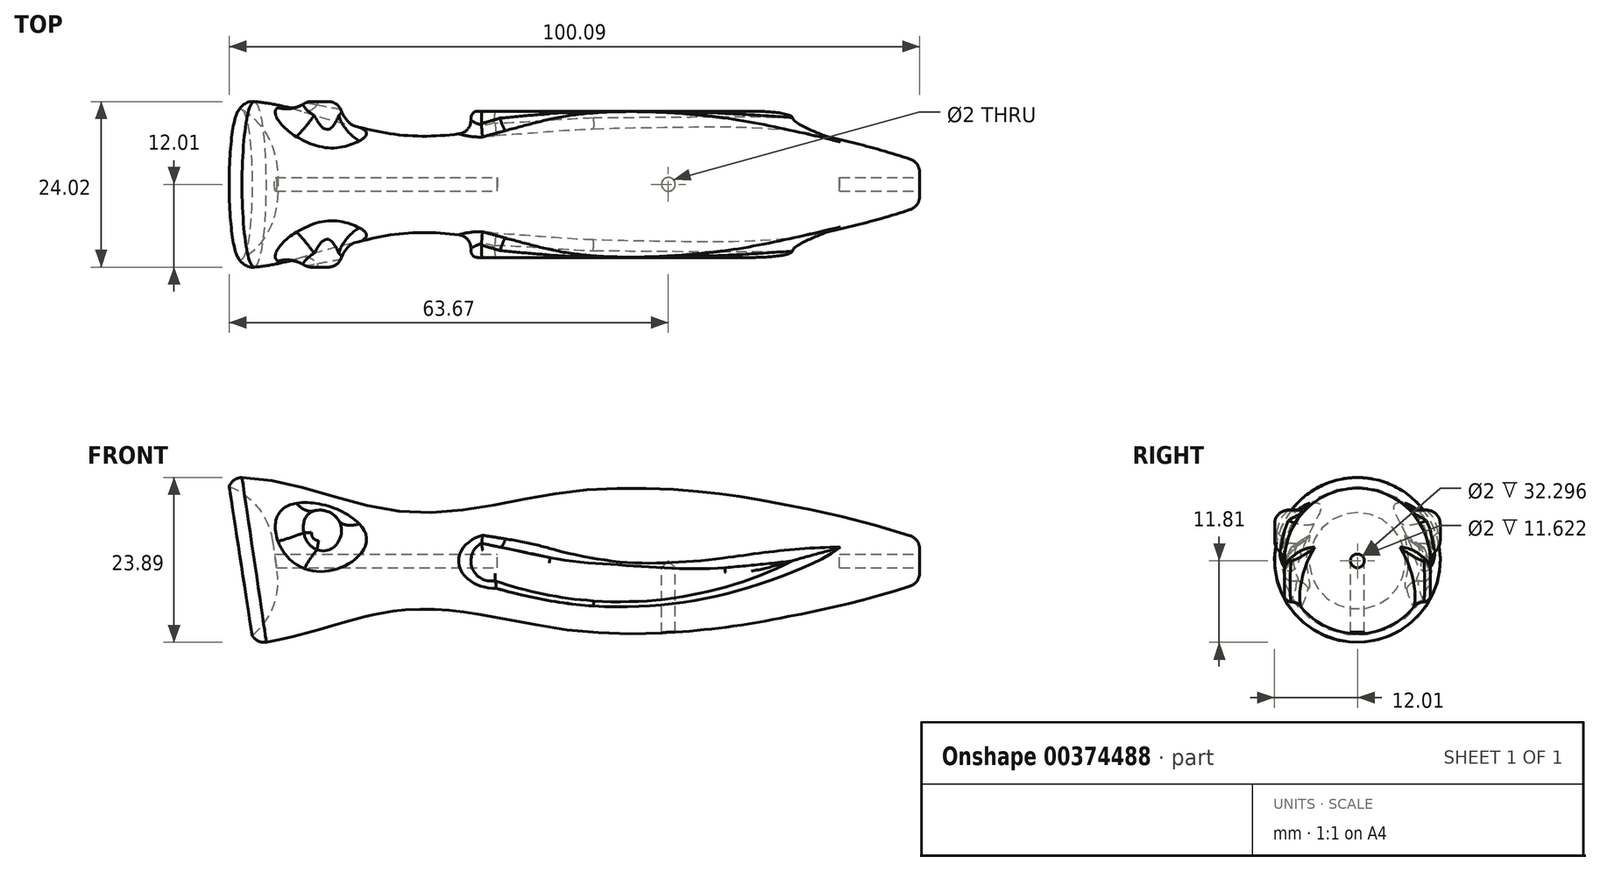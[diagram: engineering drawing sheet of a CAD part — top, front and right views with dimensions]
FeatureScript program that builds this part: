
annotation { "Feature Type Name" : "Feature", "Feature Type Description" : "" }
export const myFeature = defineFeature(function(context is Context, id is Id, definition is map)
    precondition{}
    {
        {
            var Q0;
            Q0=qCreatedBy(makeId("Front.planeOp"),FACE);
            var sketch = newSketch(context, id + "F0", { "sketchPlane" : qUnion([Q0])});
            skLineSegment(sketch, "E0", {"start": v(-64.17, 0) * mm, "end": v(44.05, 0) * mm});
            skFitSpline(sketch, "E1", {"points": [v(-64.13, 11.91) * mm, v(-39.28, 7.2) * mm, v(-14.5, 10.01) * mm, v(5.16, 9.98) * mm, v(16.36, 8.27) * mm, v(44.05, 0) * mm], "startDerivative": vector(102.28, 15.68) * mm, "endDerivative": vector(118.61, -59.18) * mm});
            skLineSegment(sketch, "E2.bottom", {"start": v(36.42, 9.8) * mm, "end": v(56.27, 9.8) * mm});
            skLineSegment(sketch, "E2.top", {"start": v(36.42, -4.91) * mm, "end": v(56.27, -4.91) * mm});
            skLineSegment(sketch, "E2.left", {"start": v(36.42, 9.8) * mm, "end": v(36.42, -4.91) * mm});
            skLineSegment(sketch, "E2.right", {"start": v(56.27, 9.8) * mm, "end": v(56.27, -4.91) * mm});
            skLineSegment(sketch, "E3", {"start": v(-64.13, 11.91) * mm, "end": v(-64.17, 0) * mm});
            skSolve(sketch);
        }
        {
            var Q0;
            {var subQ0=sQuery(id+"F0.wireOp",EDGE,"E3");Q0=makeQuery(id+"F0.imprint","IMPRINT",FACE,{"disambiguationData":[TD([[makeQuery(id+"F0.imprint","IMPRINT",EDGE,{"derivedFrom":subQ0}),1.0]])]});}
            var Q1;
            Q1 = qSketchRegion(id + "F2", true);
            var Q2;
            Q2=sQuery(id+"F0.wireOp",EDGE,"E0");
            revolve(context, id + "F1", {"surfaceOperationType" : NewSurfaceOperationType.NEW, "entities" : qUnion([Q0, Q1]), "axis" : qUnion([Q2]), "revolveType" : RevolveType.FULL});
        }
        {
            var Q0;
            Q0=qCreatedBy(makeId("Front.planeOp"),FACE);
            var sketch = newSketch(context, id + "F2", { "sketchPlane" : qUnion([Q0])});
            skLineSegment(sketch, "E4", {"start": v(-65.45, 22.3) * mm, "end": v(-56.64, -34.7) * mm});
            skLineSegment(sketch, "E5", {"start": v(-56.64, -34.7) * mm, "end": v(-81.8, -34.7) * mm});
            skLineSegment(sketch, "E6", {"start": v(-81.8, -34.7) * mm, "end": v(-65.45, 22.3) * mm});
            skSolve(sketch);
        }
        {
            var Q0;
            Q0=makeQuery(id+"F2.imprint","IMPRINT",FACE,{"disambiguationData":[TD([[makeQuery(id+"F2.imprint","IMPRINT",EDGE,{"derivedFrom":sQuery(id+"F2.wireOp",EDGE,"E4")}),-1.0]])]});
            extrude(context, id + "F3", {"entities" : qUnion([Q0]), "operationType" : NewBodyOperationType.REMOVE, "endBound" : BoundingType.SYMMETRIC, "oppositeDirection" : true, "offsetDistance" : 25 * mm, "depth" : 32.6 * mm});
        }
        {
            var Q0;
            Q0=makeQuery(id+"F3.boolean.opBoolean","COPY",FACE,{"derivedFrom":makeQuery(id+"F3.opExtrude","SWEPT_FACE",FACE,{"disambiguationData":[OSD([sQuery(id+"F2.wireOp",EDGE,"E4")])]})});
            var sketch = newSketch(context, id + "F4", { "sketchPlane" : qUnion([Q0])});
            skCircle(sketch, "E7", {"center": v(0, 9.47) * mm, "radius": 10.92 * mm});
            skSolve(sketch);
        }
        {
            var Q0;
            Q0=qSketchRegion(id+"F4",true);
            extrude(context, id + "F5", {"entities" : qUnion([Q0]), "operationType" : NewBodyOperationType.REMOVE, "oppositeDirection" : true, "offsetDistance" : 25 * mm, "depth" : 5 * mm});
        }
        {
            var Q0;
            Q0=makeQuery(id+"F5.boolean.opBoolean","COPY",EDGE,{"derivedFrom":makeQuery(id+"F5.opExtrude","CAP_EDGE",EDGE,{"disambiguationData":[OSD([sQuery(id+"F4.wireOp",EDGE,"E7")])],"isStart":false})});
            fillet(context, id + "F6", {"entities" : qUnion([Q0]), "radius" : 10 * mm, "tangentPropagation" : true, "defaultsChanged" : false, "vertexSettings" : [], "allowEdgeOverflow" : false});
        }
        {
            var Q0;
            Q0=qCreatedBy(makeId("Front.planeOp"),FACE);
            var sketch = newSketch(context, id + "F7", { "sketchPlane" : qUnion([Q0])});
            skCircle(sketch, "E8", {"center": v(-50.52, 4.14) * mm, "radius": 3.23 * mm});
            skSolve(sketch);
        }
        {
            var Q0;
            Q0=qSketchRegion(id+"F7",true);
            extrude(context, id + "F8", {"entities" : qUnion([Q0]), "operationType" : NewBodyOperationType.ADD, "endBound" : BoundingType.SYMMETRIC, "oppositeDirection" : true, "offsetDistance" : 25 * mm, "depth" : 24 * mm});
        }
        {
            var Q0;
            Q0=makeQuery(id+"F8.opExtrude","CAP_EDGE",EDGE,{"disambiguationData":[OSD([sQuery(id+"F7.wireOp",EDGE,"E8")])],"isStart":true});
            var Q1;
            Q1=makeQuery(id+"F8.opExtrude","CAP_EDGE",EDGE,{"disambiguationData":[OSD([sQuery(id+"F7.wireOp",EDGE,"E8")])],"isStart":false});
            fillet(context, id + "F9", {"entities" : qUnion([Q0, Q1]), "radius" : 2 * mm, "tangentPropagation" : true, "defaultsChanged" : false, "vertexSettings" : [], "allowEdgeOverflow" : false});
        }
        {
            var Q0;
            Q0=makeQuery(id+"F8.boolean.opBoolean","INTERSECT",EDGE,{"disambiguationData":[OD(0.0)],"derivedFrom":[makeQuery(id+"F1.opRevolve","SWEPT_FACE",FACE,{"disambiguationData":[OSD([sQuery(id+"F0.wireOp",EDGE,"E1")])]}),makeQuery(id+"F8.opExtrude","SWEPT_FACE",FACE,{"disambiguationData":[OSD([sQuery(id+"F7.wireOp",EDGE,"E8")])]})]});
            var Q1;
            Q1=makeQuery(id+"F8.boolean.opBoolean","INTERSECT",EDGE,{"disambiguationData":[OD(1.0)],"derivedFrom":[makeQuery(id+"F1.opRevolve","SWEPT_FACE",FACE,{"disambiguationData":[OSD([sQuery(id+"F0.wireOp",EDGE,"E1")])]}),makeQuery(id+"F8.opExtrude","SWEPT_FACE",FACE,{"disambiguationData":[OSD([sQuery(id+"F7.wireOp",EDGE,"E8")])]})]});
            fillet(context, id + "F10", {"entities" : qUnion([Q0, Q1]), "radius" : 5 * mm, "tangentPropagation" : true, "defaultsChanged" : false, "vertexSettings" : [], "allowEdgeOverflow" : false});
        }
        {
            var Q0;
            Q0=qCreatedBy(makeId("Front.planeOp"),FACE);
            var sketch = newSketch(context, id + "F11", { "sketchPlane" : qUnion([Q0])});
            skArc(sketch, "E9", {"start": v(-27.1, 2.57) * mm, "mid": v(-28.45, -0.99) * mm, "end": v(-25.16, -2.88) * mm});
            skArc(sketch, "E10", {"start": v(-25.16, -2.88) * mm, "mid": v(-3.29, -5.8) * mm, "end": v(18, 0) * mm});
            skArc(sketch, "E11", {"start": v(-27.1, 2.57) * mm, "mid": v(-4.66, -0.58) * mm, "end": v(18, 0) * mm});
            skSolve(sketch);
        }
        {
            var Q0;
            Q0=qSketchRegion(id+"F11",true);
            extrude(context, id + "F12", {"entities" : qUnion([Q0]), "operationType" : NewBodyOperationType.ADD, "endBound" : BoundingType.SYMMETRIC, "depth" : 21.2 * mm});
        }
        {
            var Q0;
            Q0=makeQuery(id+"F12.opExtrude","CAP_EDGE",EDGE,{"disambiguationData":[OSD([sQuery(id+"F11.wireOp",EDGE,"a57460a2-1e1d-4164-8bf6-132b992fdc75")])],"isStart":false});
            var Q1;
            Q1=makeQuery(id+"F12.opExtrude","CAP_EDGE",EDGE,{"disambiguationData":[OSD([sQuery(id+"F11.wireOp",EDGE,"QlXN6DQI-eeBz-aKKE-vuSY-wyikhmnztVA7")])],"isStart":false});
            var Q2;
            Q2=makeQuery(id+"F12.opExtrude","CAP_EDGE",EDGE,{"disambiguationData":[OSD([sQuery(id+"F11.wireOp",EDGE,"FUtrQpIp-ursx-AL5V-0rfK-VALB8NS74IF2")])],"isStart":false});
            var Q3;
            Q3=makeQuery(id+"F12.opExtrude","CAP_EDGE",EDGE,{"disambiguationData":[OSD([sQuery(id+"F11.wireOp",EDGE,"FUtrQpIp-ursx-AL5V-0rfK-VALB8NS74IF2")])],"isStart":true});
            var Q4;
            Q4=makeQuery(id+"F12.opExtrude","CAP_EDGE",EDGE,{"disambiguationData":[OSD([sQuery(id+"F11.wireOp",EDGE,"QlXN6DQI-eeBz-aKKE-vuSY-wyikhmnztVA7")])],"isStart":true});
            var Q5;
            Q5=makeQuery(id+"F12.opExtrude","CAP_EDGE",EDGE,{"disambiguationData":[OSD([sQuery(id+"F11.wireOp",EDGE,"a57460a2-1e1d-4164-8bf6-132b992fdc75")])],"isStart":true});
            var Q6;
            Q6=makeQuery(id+"F12.opExtrude","CAP_EDGE",EDGE,{"disambiguationData":[OSD([sQuery(id+"F11.wireOp",EDGE,"E11")])],"isStart":true});
            var Q7;
            Q7=makeQuery(id+"F12.opExtrude","CAP_EDGE",EDGE,{"disambiguationData":[OSD([sQuery(id+"F11.wireOp",EDGE,"E10")])],"isStart":true});
            var Q8;
            Q8=makeQuery(id+"F12.opExtrude","CAP_EDGE",EDGE,{"disambiguationData":[OSD([sQuery(id+"F11.wireOp",EDGE,"E9")])],"isStart":true});
            var Q9;
            Q9=makeQuery(id+"F12.opExtrude","CAP_EDGE",EDGE,{"disambiguationData":[OSD([sQuery(id+"F11.wireOp",EDGE,"E11")])],"isStart":false});
            var Q10;
            Q10=makeQuery(id+"F12.opExtrude","CAP_EDGE",EDGE,{"disambiguationData":[OSD([sQuery(id+"F11.wireOp",EDGE,"E9")])],"isStart":false});
            var Q11;
            Q11=makeQuery(id+"F12.opExtrude","CAP_EDGE",EDGE,{"disambiguationData":[OSD([sQuery(id+"F11.wireOp",EDGE,"E10")])],"isStart":false});
            fillet(context, id + "F13", {"entities" : qUnion([Q0, Q1, Q2, Q3, Q4, Q5, Q6, Q7, Q8, Q9, Q10, Q11]), "radius" : 1 * mm, "tangentPropagation" : true, "allowEdgeOverflow" : false});
        }
        {
            var Q0;
            Q0=makeQuery(id+"F12.boolean.opBoolean","INTERSECT",EDGE,{"disambiguationData":[OD(0.0)],"derivedFrom":[makeQuery(id+"F1.opRevolve","SWEPT_FACE",FACE,{"disambiguationData":[OSD([sQuery(id+"F0.wireOp",EDGE,"E1")])]}),makeQuery(id+"F12.opExtrude","SWEPT_FACE",FACE,{"disambiguationData":[OSD([sQuery(id+"F11.wireOp",EDGE,"FUtrQpIp-ursx-AL5V-0rfK-VALB8NS74IF2")])]})]});
            var Q1;
            Q1=makeQuery(id+"F12.boolean.opBoolean","INTERSECT",EDGE,{"disambiguationData":[OD(0.0)],"derivedFrom":[makeQuery(id+"F1.opRevolve","SWEPT_FACE",FACE,{"disambiguationData":[OSD([sQuery(id+"F0.wireOp",EDGE,"E1")])]}),makeQuery(id+"F12.opExtrude","SWEPT_FACE",FACE,{"disambiguationData":[OSD([sQuery(id+"F11.wireOp",EDGE,"a57460a2-1e1d-4164-8bf6-132b992fdc75")])]})]});
            var Q2;
            Q2=makeQuery(id+"F12.boolean.opBoolean","INTERSECT",EDGE,{"disambiguationData":[OD(1.0)],"derivedFrom":[makeQuery(id+"F1.opRevolve","SWEPT_FACE",FACE,{"disambiguationData":[OSD([sQuery(id+"F0.wireOp",EDGE,"E1")])]}),makeQuery(id+"F12.opExtrude","SWEPT_FACE",FACE,{"disambiguationData":[OSD([sQuery(id+"F11.wireOp",EDGE,"FUtrQpIp-ursx-AL5V-0rfK-VALB8NS74IF2")])]})]});
            var Q3;
            Q3=makeQuery(id+"F12.boolean.opBoolean","INTERSECT",EDGE,{"disambiguationData":[OD(1.0)],"derivedFrom":[makeQuery(id+"F1.opRevolve","SWEPT_FACE",FACE,{"disambiguationData":[OSD([sQuery(id+"F0.wireOp",EDGE,"E1")])]}),makeQuery(id+"F12.opExtrude","SWEPT_FACE",FACE,{"disambiguationData":[OSD([sQuery(id+"F11.wireOp",EDGE,"a57460a2-1e1d-4164-8bf6-132b992fdc75")])]})]});
            var Q4;
            Q4=makeQuery(id+"F12.boolean.opBoolean","INTERSECT",EDGE,{"disambiguationData":[OD(1.0)],"derivedFrom":[makeQuery(id+"F1.opRevolve","SWEPT_FACE",FACE,{"disambiguationData":[OSD([sQuery(id+"F0.wireOp",EDGE,"E1")])]}),makeQuery(id+"F12.opExtrude","SWEPT_FACE",FACE,{"disambiguationData":[OSD([sQuery(id+"F11.wireOp",EDGE,"E10")])]})]});
            var Q5;
            Q5=makeQuery(id+"F12.boolean.opBoolean","INTERSECT",EDGE,{"disambiguationData":[OD(1.0)],"derivedFrom":[makeQuery(id+"F1.opRevolve","SWEPT_FACE",FACE,{"disambiguationData":[OSD([sQuery(id+"F0.wireOp",EDGE,"E1")])]}),makeQuery(id+"F12.opExtrude","SWEPT_FACE",FACE,{"disambiguationData":[OSD([sQuery(id+"F11.wireOp",EDGE,"E9")])]})]});
            var Q6;
            Q6=makeQuery(id+"F12.boolean.opBoolean","INTERSECT",EDGE,{"disambiguationData":[OD(1.0)],"derivedFrom":[makeQuery(id+"F1.opRevolve","SWEPT_FACE",FACE,{"disambiguationData":[OSD([sQuery(id+"F0.wireOp",EDGE,"E1")])]}),makeQuery(id+"F12.opExtrude","SWEPT_FACE",FACE,{"disambiguationData":[OSD([sQuery(id+"F11.wireOp",EDGE,"E11")])]})]});
            var Q7;
            Q7=makeQuery(id+"F1.opRevolve","SWEPT_FACE",FACE,{"disambiguationData":[OSD([sQuery(id+"F0.wireOp",EDGE,"E1")])]});
            var Q8;
            Q8=makeQuery(id+"F12.boolean.opBoolean","INTERSECT",EDGE,{"disambiguationData":[OD(0.0)],"derivedFrom":[makeQuery(id+"F1.opRevolve","SWEPT_FACE",FACE,{"disambiguationData":[OSD([sQuery(id+"F0.wireOp",EDGE,"E1")])]}),makeQuery(id+"F12.opExtrude","SWEPT_FACE",FACE,{"disambiguationData":[OSD([sQuery(id+"F11.wireOp",EDGE,"E9")])]})]});
            var Q9;
            Q9=makeQuery(id+"F12.boolean.opBoolean","INTERSECT",EDGE,{"disambiguationData":[OD(0.0)],"derivedFrom":[makeQuery(id+"F1.opRevolve","SWEPT_FACE",FACE,{"disambiguationData":[OSD([sQuery(id+"F0.wireOp",EDGE,"E1")])]}),makeQuery(id+"F12.opExtrude","SWEPT_FACE",FACE,{"disambiguationData":[OSD([sQuery(id+"F11.wireOp",EDGE,"E11")])]})]});
            var Q10;
            Q10=makeQuery(id+"F12.boolean.opBoolean","INTERSECT",EDGE,{"disambiguationData":[OD(0.0)],"derivedFrom":[makeQuery(id+"F1.opRevolve","SWEPT_FACE",FACE,{"disambiguationData":[OSD([sQuery(id+"F0.wireOp",EDGE,"E1")])]}),makeQuery(id+"F12.opExtrude","SWEPT_FACE",FACE,{"disambiguationData":[OSD([sQuery(id+"F11.wireOp",EDGE,"E10")])]})]});
            fillet(context, id + "F14", {"entities" : qUnion([Q0, Q1, Q2, Q3, Q4, Q5, Q6, Q7, Q8, Q9, Q10]), "radius" : 2 * mm, "tangentPropagation" : true, "allowEdgeOverflow" : false});
        }
        {
            var Q0;
            Q0=qCreatedBy(makeId("Top.planeOp"),FACE);
            var sketch = newSketch(context, id + "F15", { "sketchPlane" : qUnion([Q0])});
            skCircle(sketch, "E12", {"center": v(0, 0) * mm, "radius": 1 * mm});
            skSolve(sketch);
        }
        {
            var Q0;
            Q0 = qSketchRegion(id + "F15", true);
            var Q1;
            Q1=sQuery(id+"F15.wireOp",EDGE,"E12");
            var Q2;
            Q2=makeQuery(id+"F1.opRevolve","SWEPT_FACE",FACE,{"disambiguationData":[OSD([sQuery(id+"F0.wireOp",EDGE,"E1")])]});
            extrude(context, id + "F16", {"entities" : qUnion([Q0]), "operationType" : NewBodyOperationType.REMOVE, "surfaceEntities" : qUnion([Q1]), "endBound" : BoundingType.UP_TO_SURFACE, "oppositeDirection" : true, "endBoundEntityFace" : qUnion([Q2]), "depth" : 38.3 * mm});
        }
        {
            var Q0;
            Q0=qCreatedBy(makeId("Right.planeOp"),FACE);
            var sketch = newSketch(context, id + "F17", { "sketchPlane" : qUnion([Q0])});
            skCircle(sketch, "E13", {"center": v(0, 0) * mm, "radius": 1 * mm});
            skSolve(sketch);
        }
        {
            var Q0;
            Q0 = qSketchRegion(id + "F17", true);
            var Q1;
            Q1=makeQuery(id+"F5.boolean.opBoolean","COPY",FACE,{"derivedFrom":makeQuery(id+"F5.opExtrude","CAP_FACE",FACE,{"disambiguationData":[OSD([sQuery(id+"F4.wireOp",EDGE,"E7")])],"isStart":false})});
            extrude(context, id + "F18", {"entities" : qUnion([Q0]), "operationType" : NewBodyOperationType.REMOVE, "endBound" : BoundingType.SYMMETRIC, "oppositeDirection" : true, "endBoundEntityFace" : qUnion([Q1]), "depth" : 151.2 * mm});
        }
        {
            var Q0;
            Q0 = qSketchRegion(id + "F17", true);
            extrude(context, id + "F19", {"entities" : qUnion([Q0]), "operationType" : NewBodyOperationType.ADD, "endBound" : BoundingType.SYMMETRIC, "depth" : 49.6 * mm});
        }
    });
